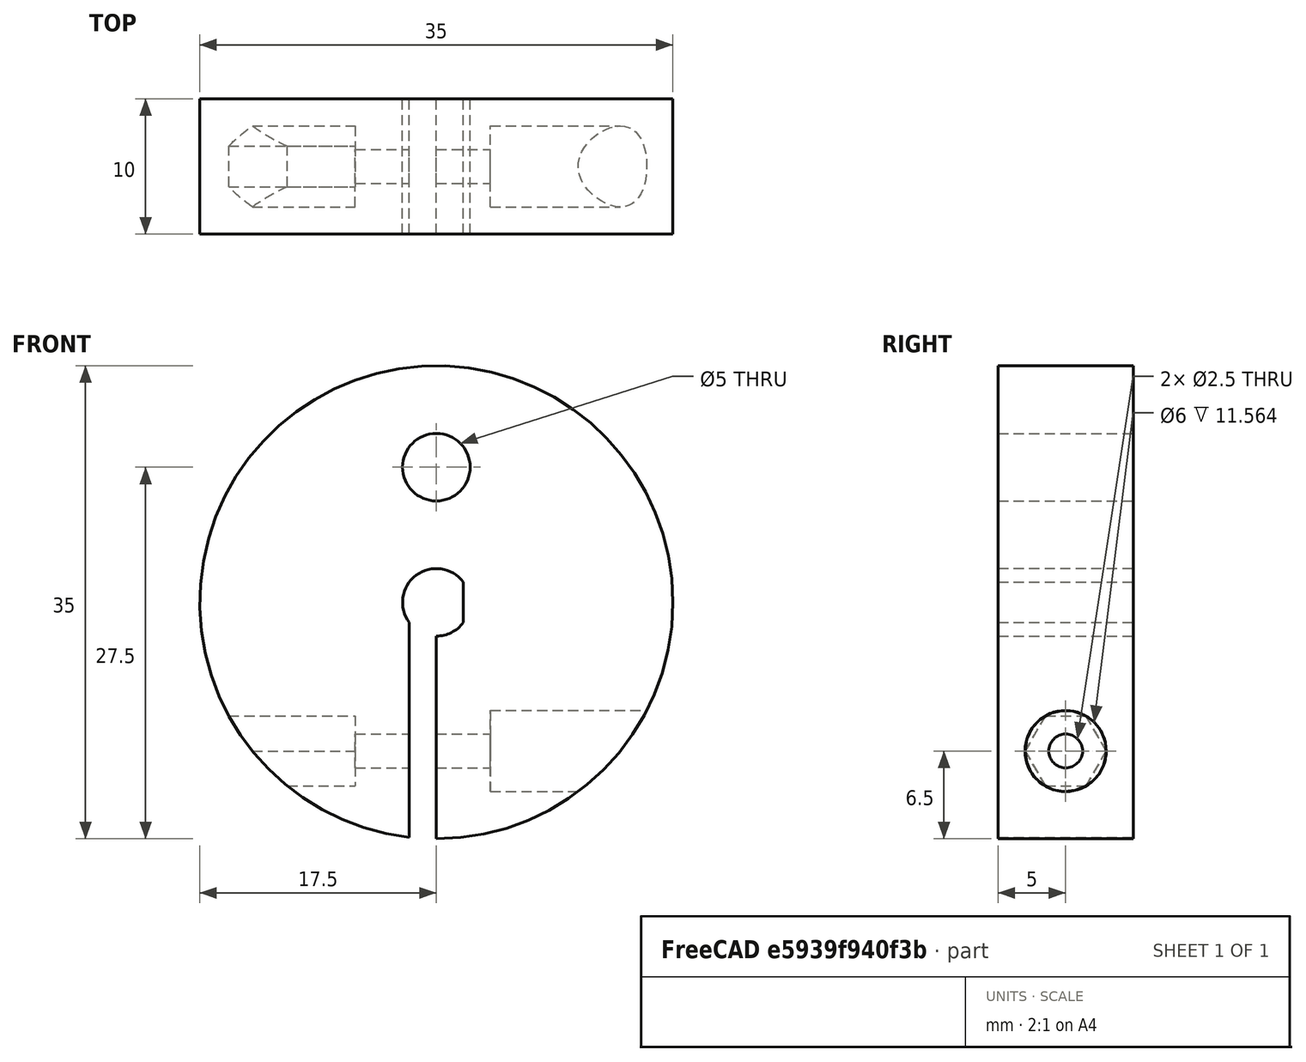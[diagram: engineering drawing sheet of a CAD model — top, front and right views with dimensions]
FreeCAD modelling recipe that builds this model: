
FCSTD DOCUMENT  (FreeCAD 0.18R16110 (Git))
Label: flywheel
License: All rights reserved
LicenseURL: http://en.wikipedia.org/wiki/All_rights_reserved
objects: Part::Cut×7, Part::Cylinder×5, Part::Box×2, Part::Prism×1, Mesh::Feature×1
note: 15 computed .brp shape members not serialized (recipe doc carries the construction recipe); baked Part::Feature solids carry a one-line shape summary decoded from their .brp

FEATURE [Part::Cylinder] Cylinder002  label="Zylinder002"
  Angle = 360
  AttacherType = Attacher::AttachEngine3D
  Height = 10
  Radius = 17.5
FEATURE [Part::Prism] Prism  label="Prisma"
  AttacherType = Attacher::AttachEngine3D
  Circumradius = 3
  Height = 10
  Placement = pos=(-16,11,5) rot=(0,1,0;1.5708rad)
  Polygon = 6
FEATURE [Part::Cylinder] Cylinder110  label="Zylinder084"
  Angle = 360
  AttacherType = Attacher::AttachEngine3D
  Height = 10
  Radius = 2.5
FEATURE [Part::Cylinder] Cylinder112  label="Zylinder085"
  Angle = 360
  AttacherType = Attacher::AttachEngine3D
  Height = 13
  Placement = pos=(4,11,5) rot=(0,1,0;1.5708rad)
  Radius = 3
FEATURE [Part::Cylinder] Cylinder009  label="Zylinder009"
  Angle = 360
  AttacherType = Attacher::AttachEngine3D
  Height = 15
  Placement = pos=(0,-10,-5) rot=(0,0,1;0rad)
  Radius = 2.5
FEATURE [Part::Cut] Cut005  label="Schwungscheibe"
  Base = -> Cylinder002
  Tool = -> Cylinder009
FEATURE [Part::Box] Box034  label="Quader028"
  AttacherType = Attacher::AttachEngine3D
  Height = 10
  Length = 10
  Placement = pos=(2,-4,0) rot=(0,0,1;0rad)
  Width = 10
FEATURE [Part::Cut] Cut136  label="achse1"
  Base = -> Cylinder110
  Tool = -> Box034
FEATURE [Part::Cut] Cut137  label="Schwungscheibe001"
  Base = -> Cut005
  Tool = -> Cut136
FEATURE [Part::Box] Box035  label="Quader029"
  AttacherType = Attacher::AttachEngine3D
  Height = 10
  Length = 2
  Placement = pos=(-2,1,0) rot=(0,0,1;0rad)
  Width = 17
FEATURE [Part::Cut] Cut138  label="Schwungscheibe002"
  Base = -> Cut137
  Tool = -> Box035
FEATURE [Part::Cylinder] Cylinder111  label="Zylinder"
  Angle = 360
  AttacherType = Attacher::AttachEngine3D
  Height = 30
  Placement = pos=(-15,11,5) rot=(0,1,0;1.5708rad)
  Radius = 1.25
FEATURE [Part::Cut] Cut139
  Base = -> Cut138
  Tool = -> Cylinder111
FEATURE [Part::Cut] Cut140  label="Schwungscheibe003"
  Base = -> Cut139
  Tool = -> Cylinder112
FEATURE [Part::Cut] Cut141  label="Schwungscheibe004"
  Base = -> Cut140
  Placement = pos=(0,8,44) rot=(-1,0,0;1.5708rad)
  Tool = -> Prism
FEATURE [Mesh::Feature] Mesh  label="Schwungscheibe004 (Meshed)"
